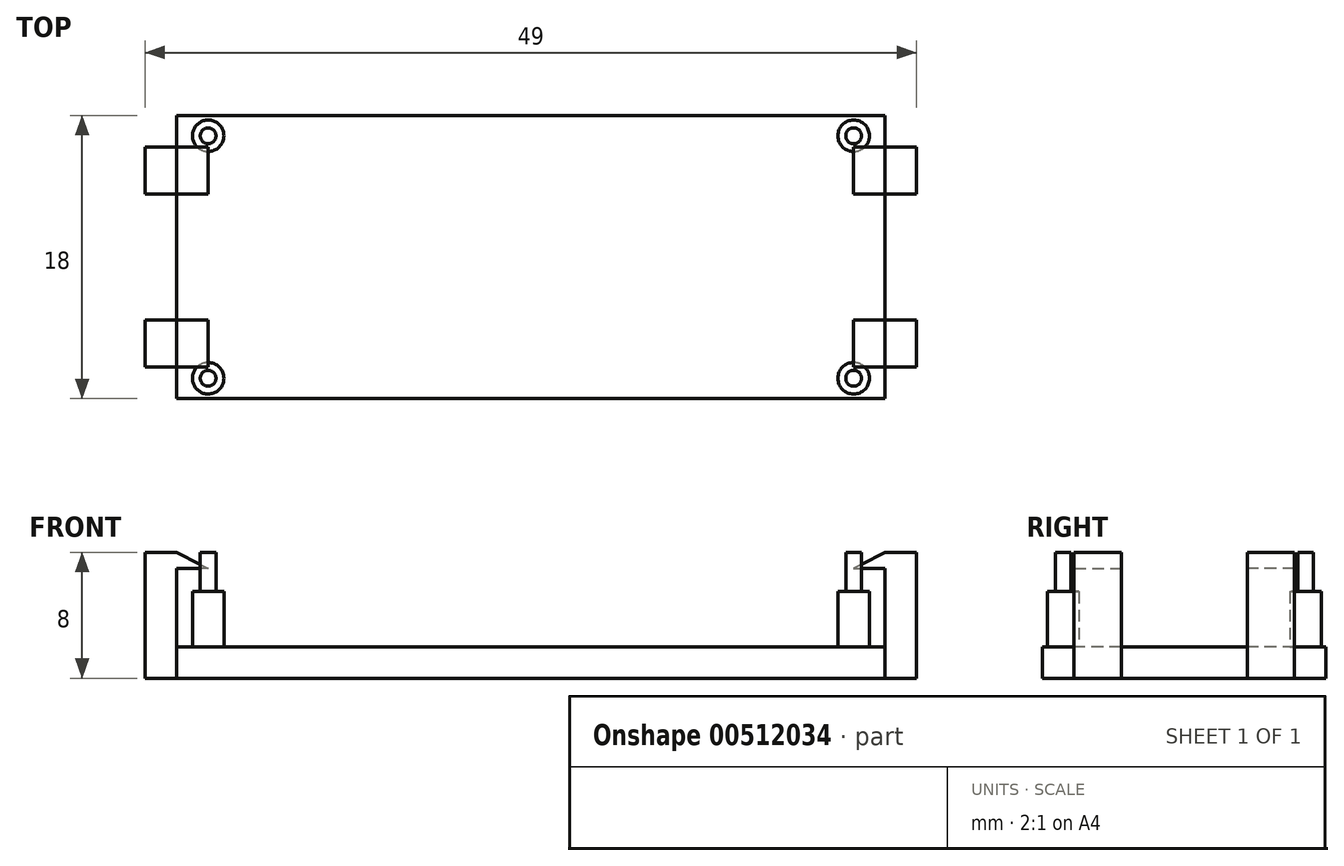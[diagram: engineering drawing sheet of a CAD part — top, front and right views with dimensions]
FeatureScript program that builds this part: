
annotation { "Feature Type Name" : "Feature", "Feature Type Description" : "" }
export const myFeature = defineFeature(function(context is Context, id is Id, definition is map)
    precondition{}
    {
        {
            var Q0;
            Q0=qCreatedBy(makeId("Top.planeOp"),FACE);
            var sketch = newSketch(context, id + "F0", { "sketchPlane" : qUnion([Q0])});
            skLineSegment(sketch, "E0.bottom", {"start": v(-22.5, 9) * mm, "end": v(22.5, 9) * mm});
            skLineSegment(sketch, "E0.top", {"start": v(-22.5, -9) * mm, "end": v(22.5, -9) * mm});
            skLineSegment(sketch, "E0.left", {"start": v(-22.5, 9) * mm, "end": v(-22.5, -9) * mm});
            skLineSegment(sketch, "E0.right", {"start": v(22.5, 9) * mm, "end": v(22.5, -9) * mm});
            skPoint(sketch, "E0.middle", {"position": v(0, 0) * mm});
            skCircle(sketch, "E1", {"center": v(-20.5, 7.7) * mm, "radius": 1 * mm});
            skCircle(sketch, "E2", {"center": v(20.5, 7.7) * mm, "radius": 1 * mm});
            skCircle(sketch, "E3", {"center": v(20.5, -7.7) * mm, "radius": 1 * mm});
            skCircle(sketch, "E4", {"center": v(-20.5, -7.7) * mm, "radius": 1 * mm});
            skCircle(sketch, "E5", {"center": v(-20.5, 7.7) * mm, "radius": 0.5 * mm});
            skCircle(sketch, "E6", {"center": v(20.5, 7.7) * mm, "radius": 0.5 * mm});
            skCircle(sketch, "E7", {"center": v(20.5, -7.7) * mm, "radius": 0.5 * mm});
            skCircle(sketch, "E8", {"center": v(-20.5, -7.7) * mm, "radius": 0.5 * mm});
            skLineSegment(sketch, "E9.bottom", {"start": v(22.5, 7) * mm, "end": v(24.5, 7) * mm});
            skLineSegment(sketch, "E9.top", {"start": v(22.5, 4) * mm, "end": v(24.5, 4) * mm});
            skLineSegment(sketch, "E9.left", {"start": v(22.5, 7) * mm, "end": v(22.5, 4) * mm});
            skLineSegment(sketch, "E9.right", {"start": v(24.5, 7) * mm, "end": v(24.5, 4) * mm});
            skLineSegment(sketch, "E10.bottom", {"start": v(-22.5, 7) * mm, "end": v(-24.5, 7) * mm});
            skLineSegment(sketch, "E10.top", {"start": v(-22.5, 4) * mm, "end": v(-24.5, 4) * mm});
            skLineSegment(sketch, "E10.left", {"start": v(-22.5, 7) * mm, "end": v(-22.5, 4) * mm});
            skLineSegment(sketch, "E10.right", {"start": v(-24.5, 7) * mm, "end": v(-24.5, 4) * mm});
            skLineSegment(sketch, "E11.bottom", {"start": v(-22.5, -7) * mm, "end": v(-24.5, -7) * mm});
            skLineSegment(sketch, "E11.top", {"start": v(-22.5, -4) * mm, "end": v(-24.5, -4) * mm});
            skLineSegment(sketch, "E11.left", {"start": v(-22.5, -7) * mm, "end": v(-22.5, -4) * mm});
            skLineSegment(sketch, "E11.right", {"start": v(-24.5, -7) * mm, "end": v(-24.5, -4) * mm});
            skLineSegment(sketch, "E12.bottom", {"start": v(22.5, -7) * mm, "end": v(24.5, -7) * mm});
            skLineSegment(sketch, "E12.top", {"start": v(22.5, -4) * mm, "end": v(24.5, -4) * mm});
            skLineSegment(sketch, "E12.left", {"start": v(22.5, -7) * mm, "end": v(22.5, -4) * mm});
            skLineSegment(sketch, "E12.right", {"start": v(24.5, -7) * mm, "end": v(24.5, -4) * mm});
            skSolve(sketch);
        }
        {
            var Q0;
            {var subQ5=sQuery(id+"F0.wireOp",EDGE,"E0.bottom");Q0=makeQuery(id+"F0.imprint","IMPRINT",FACE,{"disambiguationData":[TD([[makeQuery(id+"F0.imprint","IMPRINT",EDGE,{"derivedFrom":subQ5}),-1.0]])]});}
            var Q1;
            {var subQ0=sQuery(id+"F0.wireOp",EDGE,"ooETt2bT-4Bjj-iyFL-skqx-cBnWY95XIXnE.left");Q1=makeQuery(id+"F0.imprint","IMPRINT",FACE,{"disambiguationData":[TD([[makeQuery(id+"F0.imprint","IMPRINT",EDGE,{"derivedFrom":subQ0}),1.0]])]});}
            var Q2;
            {var subQ0=sQuery(id+"F0.wireOp",EDGE,"upHGcy0h-ldb7-zxNg-2YdD-Idfr9pYvQREv.left");Q2=makeQuery(id+"F0.imprint","IMPRINT",FACE,{"disambiguationData":[TD([[makeQuery(id+"F0.imprint","IMPRINT",EDGE,{"derivedFrom":subQ0}),1.0]])]});}
            var Q3;
            Q3=makeQuery(id+"F0.imprint","IMPRINT",FACE,{"disambiguationData":[TD([[makeQuery(id+"F0.imprint","IMPRINT",EDGE,{"derivedFrom":sQuery(id+"F0.wireOp",EDGE,"E1")}),1.0]])]});
            var Q4;
            Q4=makeQuery(id+"F0.imprint","IMPRINT",FACE,{"disambiguationData":[TD([[makeQuery(id+"F0.imprint","IMPRINT",EDGE,{"derivedFrom":sQuery(id+"F0.wireOp",EDGE,"E5")}),1.0]])]});
            var Q5;
            Q5=makeQuery(id+"F0.imprint","IMPRINT",FACE,{"disambiguationData":[TD([[makeQuery(id+"F0.imprint","IMPRINT",EDGE,{"derivedFrom":sQuery(id+"F0.wireOp",EDGE,"E6")}),1.0]])]});
            var Q6;
            Q6=makeQuery(id+"F0.imprint","IMPRINT",FACE,{"disambiguationData":[TD([[makeQuery(id+"F0.imprint","IMPRINT",EDGE,{"derivedFrom":sQuery(id+"F0.wireOp",EDGE,"E2")}),1.0]])]});
            var Q7;
            Q7=makeQuery(id+"F0.imprint","IMPRINT",FACE,{"disambiguationData":[TD([[makeQuery(id+"F0.imprint","IMPRINT",EDGE,{"derivedFrom":sQuery(id+"F0.wireOp",EDGE,"E3")}),1.0]])]});
            var Q8;
            Q8=makeQuery(id+"F0.imprint","IMPRINT",FACE,{"disambiguationData":[TD([[makeQuery(id+"F0.imprint","IMPRINT",EDGE,{"derivedFrom":sQuery(id+"F0.wireOp",EDGE,"E7")}),1.0]])]});
            var Q9;
            Q9=makeQuery(id+"F0.imprint","IMPRINT",FACE,{"disambiguationData":[TD([[makeQuery(id+"F0.imprint","IMPRINT",EDGE,{"derivedFrom":sQuery(id+"F0.wireOp",EDGE,"E4")}),1.0]])]});
            var Q10;
            Q10=makeQuery(id+"F0.imprint","IMPRINT",FACE,{"disambiguationData":[TD([[makeQuery(id+"F0.imprint","IMPRINT",EDGE,{"derivedFrom":sQuery(id+"F0.wireOp",EDGE,"E8")}),1.0]])]});
            extrude(context, id + "F1", {"entities" : qUnion([Q0, Q1, Q2, Q3, Q4, Q5, Q6, Q7, Q8, Q9, Q10]), "depth" : 2 * mm, "offsetDistance" : 25 * mm});
        }
        {
            var Q0;
            Q0=makeQuery(id+"F0.imprint","IMPRINT",FACE,{"disambiguationData":[TD([[makeQuery(id+"F0.imprint","IMPRINT",EDGE,{"derivedFrom":sQuery(id+"F0.wireOp",EDGE,"E1")}),1.0]])]});
            var Q1;
            Q1=makeQuery(id+"F0.imprint","IMPRINT",FACE,{"disambiguationData":[TD([[makeQuery(id+"F0.imprint","IMPRINT",EDGE,{"derivedFrom":sQuery(id+"F0.wireOp",EDGE,"E5")}),1.0]])]});
            var Q2;
            Q2=makeQuery(id+"F0.imprint","IMPRINT",FACE,{"disambiguationData":[TD([[makeQuery(id+"F0.imprint","IMPRINT",EDGE,{"derivedFrom":sQuery(id+"F0.wireOp",EDGE,"E4")}),1.0]])]});
            var Q3;
            Q3=makeQuery(id+"F0.imprint","IMPRINT",FACE,{"disambiguationData":[TD([[makeQuery(id+"F0.imprint","IMPRINT",EDGE,{"derivedFrom":sQuery(id+"F0.wireOp",EDGE,"E8")}),1.0]])]});
            var Q4;
            Q4=makeQuery(id+"F0.imprint","IMPRINT",FACE,{"disambiguationData":[TD([[makeQuery(id+"F0.imprint","IMPRINT",EDGE,{"derivedFrom":sQuery(id+"F0.wireOp",EDGE,"E2")}),1.0]])]});
            var Q5;
            Q5=makeQuery(id+"F0.imprint","IMPRINT",FACE,{"disambiguationData":[TD([[makeQuery(id+"F0.imprint","IMPRINT",EDGE,{"derivedFrom":sQuery(id+"F0.wireOp",EDGE,"E6")}),1.0]])]});
            var Q6;
            Q6=makeQuery(id+"F0.imprint","IMPRINT",FACE,{"disambiguationData":[TD([[makeQuery(id+"F0.imprint","IMPRINT",EDGE,{"derivedFrom":sQuery(id+"F0.wireOp",EDGE,"E3")}),1.0]])]});
            var Q7;
            Q7=makeQuery(id+"F0.imprint","IMPRINT",FACE,{"disambiguationData":[TD([[makeQuery(id+"F0.imprint","IMPRINT",EDGE,{"derivedFrom":sQuery(id+"F0.wireOp",EDGE,"E7")}),1.0]])]});
            extrude(context, id + "F2", {"entities" : qUnion([Q0, Q1, Q2, Q3, Q4, Q5, Q6, Q7]), "operationType" : NewBodyOperationType.ADD, "depth" : 5.5 * mm, "offsetDistance" : 25 * mm});
        }
        {
            var Q0;
            Q0=makeQuery(id+"F0.imprint","IMPRINT",FACE,{"disambiguationData":[TD([[makeQuery(id+"F0.imprint","IMPRINT",EDGE,{"derivedFrom":sQuery(id+"F0.wireOp",EDGE,"E5")}),1.0]])]});
            var Q1;
            Q1=makeQuery(id+"F0.imprint","IMPRINT",FACE,{"disambiguationData":[TD([[makeQuery(id+"F0.imprint","IMPRINT",EDGE,{"derivedFrom":sQuery(id+"F0.wireOp",EDGE,"E6")}),1.0]])]});
            var Q2;
            Q2=makeQuery(id+"F0.imprint","IMPRINT",FACE,{"disambiguationData":[TD([[makeQuery(id+"F0.imprint","IMPRINT",EDGE,{"derivedFrom":sQuery(id+"F0.wireOp",EDGE,"E7")}),1.0]])]});
            var Q3;
            Q3=makeQuery(id+"F0.imprint","IMPRINT",FACE,{"disambiguationData":[TD([[makeQuery(id+"F0.imprint","IMPRINT",EDGE,{"derivedFrom":sQuery(id+"F0.wireOp",EDGE,"E8")}),1.0]])]});
            extrude(context, id + "F3", {"entities" : qUnion([Q0, Q1, Q2, Q3]), "operationType" : NewBodyOperationType.ADD, "depth" : 8 * mm, "offsetDistance" : 25 * mm});
        }
        {
            var Q0;
            Q0=makeQuery(id+"F0.imprint","IMPRINT",FACE,{"disambiguationData":[TD([[makeQuery(id+"F0.imprint","IMPRINT",EDGE,{"derivedFrom":sQuery(id+"F0.wireOp",EDGE,"E10.bottom")}),1.0]])]});
            extrude(context, id + "F4", {"entities" : qUnion([Q0]), "depth" : 8 * mm, "offsetDistance" : 25 * mm});
        }
        {
            var Q0;
            Q0=makeQuery(id+"F4.opExtrude","SWEPT_FACE",FACE,{"disambiguationData":[OSD([sQuery(id+"F0.wireOp",EDGE,"E10.top")])]});
            var sketch = newSketch(context, id + "F5", { "sketchPlane" : qUnion([Q0])});
            skLineSegment(sketch, "E13", {"start": v(-22.5, 6.98) * mm, "end": v(-20.5, 6.98) * mm});
            skLineSegment(sketch, "E14", {"start": v(-20.5, 6.98) * mm, "end": v(-22.5, 8) * mm});
            skSolve(sketch);
        }
        {
            var Q0;
            {var subQ0=sQuery(id+"F5.wireOp",EDGE,"E13");Q0=makeQuery(id+"F5.imprint","IMPRINT",FACE,{"disambiguationData":[TD([[makeQuery(id+"F5.imprint","IMPRINT",EDGE,{"derivedFrom":subQ0}),1.0]])]});}
            var Q1;
            Q1=makeQuery(id+"F4.opExtrude","SWEPT_FACE",FACE,{"disambiguationData":[OSD([sQuery(id+"F0.wireOp",EDGE,"E10.bottom")])]});
            extrude(context, id + "F6", {"entities" : qUnion([Q0]), "operationType" : NewBodyOperationType.ADD, "endBound" : BoundingType.UP_TO_SURFACE, "oppositeDirection" : true, "depth" : 25 * mm, "endBoundEntityFace" : qUnion([Q1]), "offsetDistance" : 25 * mm});
        }
        {
            var Q0;
            Q0=makeQuery(id+"F4.opExtrude","SWEPT_BODY",BODY,{"disambiguationData":[OSD([sQuery(id+"F0.wireOp",EDGE,"E10.bottom"),sQuery(id+"F0.wireOp",EDGE,"E10.top"),sQuery(id+"F0.wireOp",EDGE,"E10.left"),sQuery(id+"F0.wireOp",EDGE,"E10.right")])]});
            var Q1;
            Q1=qCreatedBy(makeId("Front.planeOp"),FACE);
            mirror(context, id + "F7", {"entities" : qUnion([Q0]), "mirrorPlane" : qUnion([Q1])});
        }
        {
            var Q0;
            Q0=makeQuery(id+"F4.opExtrude","SWEPT_BODY",BODY,{"disambiguationData":[OSD([sQuery(id+"F0.wireOp",EDGE,"E10.bottom"),sQuery(id+"F0.wireOp",EDGE,"E10.top"),sQuery(id+"F0.wireOp",EDGE,"E10.left"),sQuery(id+"F0.wireOp",EDGE,"E10.right")])]});
            var Q1;
            Q1=makeQuery(id+"F7.opPattern","COPY",BODY,{"derivedFrom":makeQuery(id+"F4.opExtrude","SWEPT_BODY",BODY,{"disambiguationData":[OSD([sQuery(id+"F0.wireOp",EDGE,"E10.bottom"),sQuery(id+"F0.wireOp",EDGE,"E10.top"),sQuery(id+"F0.wireOp",EDGE,"E10.left"),sQuery(id+"F0.wireOp",EDGE,"E10.right")])]}),"instanceName":"1"});
            var Q2;
            Q2=qCreatedBy(makeId("Right.planeOp"),FACE);
            mirror(context, id + "F8", {"operationType" : NewBodyOperationType.ADD, "entities" : qUnion([Q0, Q1]), "mirrorPlane" : qUnion([Q2])});
        }
    });
